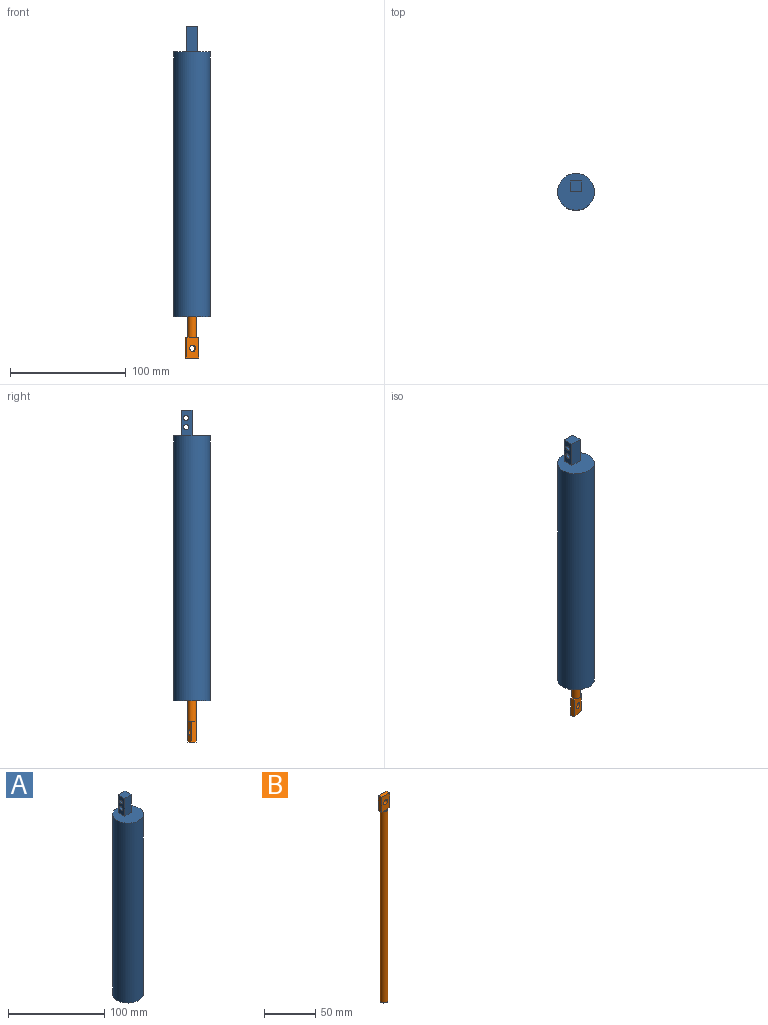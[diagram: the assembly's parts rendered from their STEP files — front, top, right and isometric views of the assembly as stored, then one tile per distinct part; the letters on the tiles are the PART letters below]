
ASSEMBLY  parts=2 mates=1
PART A: 12 faces, bbox 31.8x31.8x251 mm
  f0: plane 31.75x31.75mm, normal (0,0,1), area 697.5mm2, adj f1,f3,f4,f5,f6
  f1: cylinder r=15.88mm len=228.6mm, axis (0,0,1), area 22801.8mm2, adj f0,f2
  f2: plane 31.75x31.75mm, normal (0,0,-1), area 746.1mm2, adj f1,f10
  f3: plane 22.43x10.16mm, normal (0,1,0), area 227.9mm2, adj f0,f4,f6,f7
  f4: plane 22.43x9.27mm, normal (-1,0,0), area 179mm2, adj f0,f3,f5,f7,f8,f9
  f5: plane 22.43x10.16mm, normal (0,-1,0), area 227.9mm2, adj f0,f4,f6,f7
  f6: plane 22.43x9.27mm, normal (1,0,0), area 179mm2, adj f0,f3,f5,f7,f8,f9
  f7: plane 10.16x9.27mm, normal (0,0,1), area 94.2mm2, adj f3,f4,f5,f6
  f8: cylinder r=2.15mm len=10.16mm, axis (1,0,0), area 137mm2, adj f4,f6
  f9: cylinder r=2.15mm len=10.16mm, axis (1,0,0), area 137mm2, adj f4,f6
  f10: cylinder r=3.81mm len=203.2mm, axis (0,0,-1), area 4864.4mm2, adj f2,f11
  f11: plane 7.62x7.62mm, normal (0,0,-1), area 45.6mm2, adj f10
PART B: 12 faces, bbox 11.2x7.5x246.4 mm
  f0: plane 6.17x1.6mm, normal (0,0,1), area 6.9mm2, adj f1,f6
  f1: cylinder r=3.77mm len=228.6mm, axis (0,0,-1), area 5417.7mm2, adj f0,f2,f3,f4,f5
  f2: plane 6.17x1.6mm, normal (0,0,1), area 6.9mm2, adj f1,f8
  f3: plane 7.54x7.54mm, normal (0,0,-1), area 44.7mm2, adj f1
  f4: plane 4.34x2.5mm, normal (0,0,-1), area 8.8mm2, adj f1,f6,f8,f9
  f5: plane 4.34x2.5mm, normal (0,0,-1), area 8.8mm2, adj f1,f6,f7,f8
  f6: plane 17.78x11.18mm, normal (0,-1,0), area 176.4mm2, adj f0,f4,f5,f7,f9,f10,f11
  f7: plane 17.78x4.34mm, normal (1,0,0), area 77.2mm2, adj f5,f6,f8,f10
  f8: plane 17.78x11.18mm, normal (0,1,0), area 176.4mm2, adj f2,f4,f5,f7,f9,f10,f11
  f9: plane 17.78x4.34mm, normal (-1,0,0), area 77.2mm2, adj f4,f6,f8,f10
  f10: plane 11.18x4.34mm, normal (0,0,1), area 48.5mm2, adj f6,f7,f8,f9
  f11: cylinder r=2.67mm len=5.33mm, axis (0,1,0), area 72.8mm2, adj f6,f8
PLACE A at identity fixed
PLACE B rot(axis=(-0.99,-0.12,0),180deg) t=(0,0,-17.78)mm
MATE cylindrical A.f10 <-> B.f1  axis (0,0,-1) through (0,0,-127)mm
